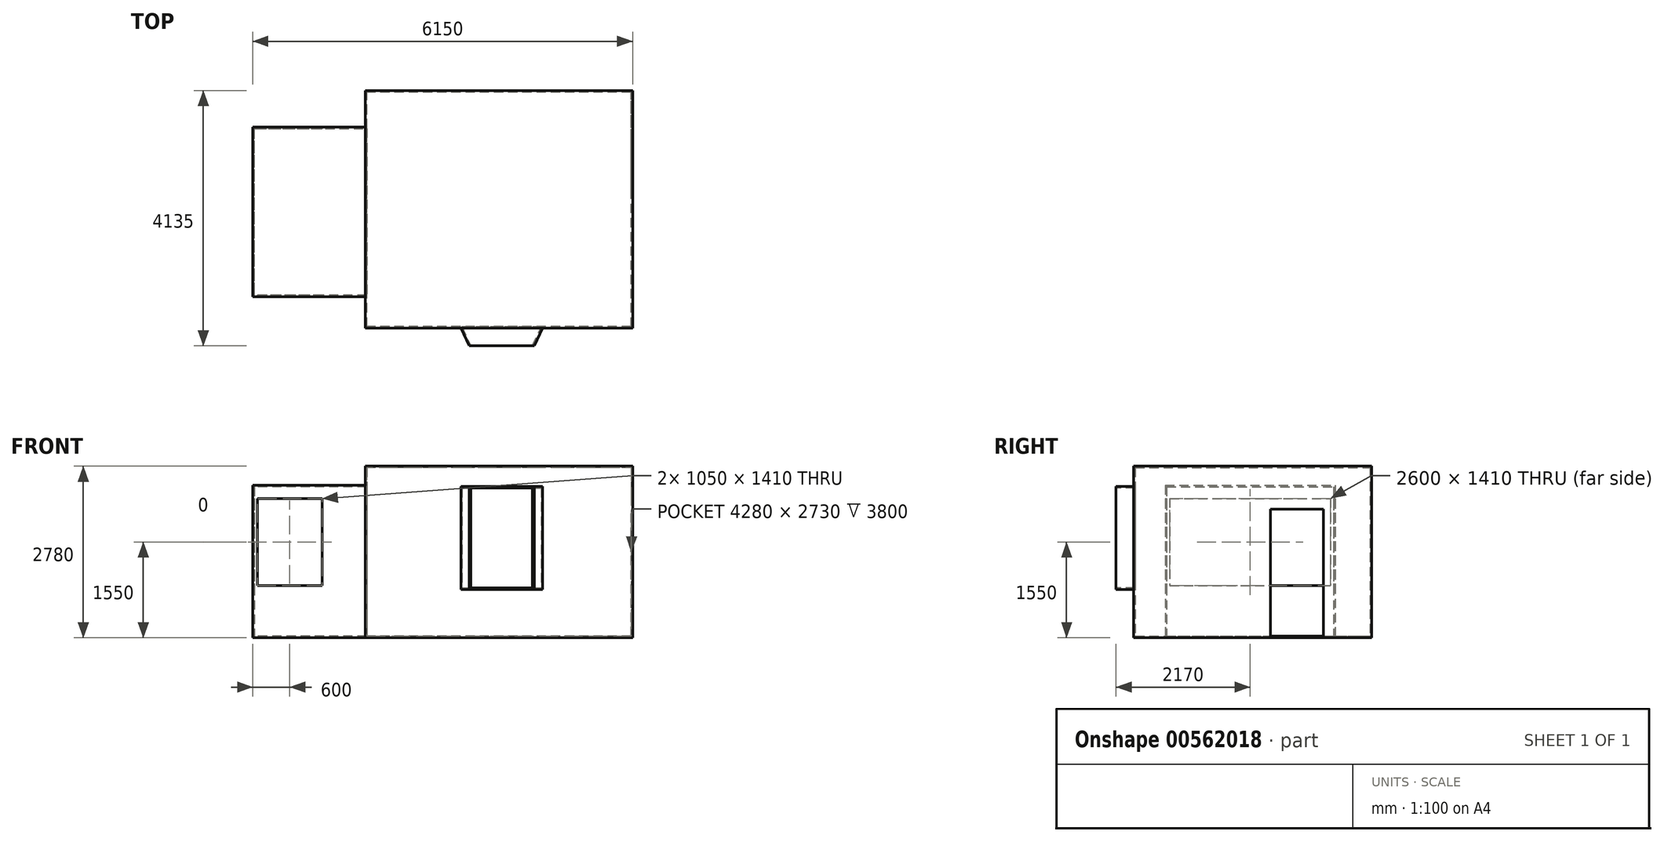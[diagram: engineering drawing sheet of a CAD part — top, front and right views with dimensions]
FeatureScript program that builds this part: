
annotation { "Feature Type Name" : "Feature", "Feature Type Description" : "" }
export const myFeature = defineFeature(function(context is Context, id is Id, definition is map)
    precondition{}
    {
        {
            var Q0;
            Q0=qCreatedBy(makeId("Top.planeOp"),FACE);
            var sketch = newSketch(context, id + "F0", { "sketchPlane" : qUnion([Q0])});
            skLineSegment(sketch, "E0.bottom", {"start": v(0, 0) * mm, "end": v(-1450, 0) * mm});
            skLineSegment(sketch, "E0.top", {"start": v(0, 3800) * mm, "end": v(-4280, 3800) * mm});
            skLineSegment(sketch, "E0.left", {"start": v(0, 0) * mm, "end": v(0, 3800) * mm});
            skLineSegment(sketch, "E0.right", {"start": v(-4280, 0) * mm, "end": v(-4280, 510) * mm});
            skLineSegment(sketch, "E1", {"start": v(-4280, 510) * mm, "end": v(-6100, 510) * mm});
            skLineSegment(sketch, "E2", {"start": v(-6100, 510) * mm, "end": v(-6100, 3210) * mm});
            skLineSegment(sketch, "E3", {"start": v(-6100, 3210) * mm, "end": v(-4280, 3210) * mm});
            skLineSegment(sketch, "E4.trimOffspring", {"start": v(-4280, 3210) * mm, "end": v(-4280, 3800) * mm});
            skLineSegment(sketch, "E5", {"start": v(-2740, 0) * mm, "end": v(-2595, -310) * mm});
            skLineSegment(sketch, "E6", {"start": v(-2595, -310) * mm, "end": v(-1595, -310) * mm});
            skLineSegment(sketch, "E7", {"start": v(-1595, -310) * mm, "end": v(-1450, 0) * mm});
            skLineSegment(sketch, "E8.trimOffspring", {"start": v(-2740, 0) * mm, "end": v(-4280, 0) * mm});
            skSolve(sketch);
        }
        {
            var Q0;
            Q0=makeQuery(id+"F0.imprint","IMPRINT",FACE,{"disambiguationData":[TD([[makeQuery(id+"F0.imprint","IMPRINT",EDGE,{"derivedFrom":sQuery(id+"F0.wireOp",EDGE,"E0.bottom")}),-1.0]])]});
            extrude(context, id + "F1", {"entities" : qUnion([Q0]), "depth" : 2730 * mm, "offsetDistance" : 25 * mm});
        }
        {
            var Q0;
            Q0=makeQuery(id+"F1.opExtrude","CAP_FACE",FACE,{"disambiguationData":[OSD([sQuery(id+"F0.wireOp",EDGE,"E0.bottom"),sQuery(id+"F0.wireOp",EDGE,"E0.top"),sQuery(id+"F0.wireOp",EDGE,"E0.left"),sQuery(id+"F0.wireOp",EDGE,"E0.right"),sQuery(id+"F0.wireOp",EDGE,"E1"),sQuery(id+"F0.wireOp",EDGE,"E2"),sQuery(id+"F0.wireOp",EDGE,"E3"),sQuery(id+"F0.wireOp",EDGE,"E4.trimOffspring"),sQuery(id+"F0.wireOp",EDGE,"E5"),sQuery(id+"F0.wireOp",EDGE,"E6"),sQuery(id+"F0.wireOp",EDGE,"E7"),sQuery(id+"F0.wireOp",EDGE,"E8.trimOffspring")])],"isStart":true});
            var sketch = newSketch(context, id + "F2", { "sketchPlane" : qUnion([Q0])});
            skLineSegment(sketch, "E9", {"start": v(-2740, 0) * mm, "end": v(-1450, 0) * mm});
            skLineSegment(sketch, "E10", {"start": v(-1450, 0) * mm, "end": v(-1595, 310) * mm});
            skLineSegment(sketch, "E11", {"start": v(-1595, 310) * mm, "end": v(-2595, 310) * mm});
            skLineSegment(sketch, "E12", {"start": v(-2595, 310) * mm, "end": v(-2740, 0) * mm});
            skSolve(sketch);
        }
        {
            var Q0;
            Q0 = qSketchRegion(id + "F2", true);
            var Q1;
            Q1=makeQuery(id+"F2.imprint","IMPRINT",FACE,{"disambiguationData":[TD([[makeQuery(id+"F2.imprint","IMPRINT",EDGE,{"derivedFrom":sQuery(id+"F2.wireOp",EDGE,"E9")}),1.0]])]});
            extrude(context, id + "F3", {"entities" : qUnion([Q0, Q1]), "operationType" : NewBodyOperationType.REMOVE, "oppositeDirection" : true, "depth" : 780 * mm, "offsetDistance" : 25 * mm});
        }
        {
            var Q0;
            Q0=makeQuery(id+"F1.opExtrude","CAP_FACE",FACE,{"disambiguationData":[OSD([sQuery(id+"F0.wireOp",EDGE,"E0.bottom"),sQuery(id+"F0.wireOp",EDGE,"E0.top"),sQuery(id+"F0.wireOp",EDGE,"E0.left"),sQuery(id+"F0.wireOp",EDGE,"E0.right"),sQuery(id+"F0.wireOp",EDGE,"E1"),sQuery(id+"F0.wireOp",EDGE,"E2"),sQuery(id+"F0.wireOp",EDGE,"E3"),sQuery(id+"F0.wireOp",EDGE,"E4.trimOffspring"),sQuery(id+"F0.wireOp",EDGE,"E5"),sQuery(id+"F0.wireOp",EDGE,"E6"),sQuery(id+"F0.wireOp",EDGE,"E7"),sQuery(id+"F0.wireOp",EDGE,"E8.trimOffspring")])],"isStart":true});
            cPlane(context, id + "F4", {"entities" : qUnion([Q0]), "cplaneType" : CPlaneType.OFFSET, "offset" : 2400 * mm, "oppositeDirection" : true, "width" : 150 * mm, "height" : 150 * mm});
        }
        {
            var Q0;
            Q0=qCreatedBy(id+"F4.planeOp",FACE);
            var sketch = newSketch(context, id + "F5", { "sketchPlane" : qUnion([Q0])});
            skLineSegment(sketch, "E13.0", {"start": v(-2740, 0) * mm, "end": v(-2595, 310) * mm});
            skLineSegment(sketch, "E14.0", {"start": v(-2595, 310) * mm, "end": v(-1595, 310) * mm});
            skLineSegment(sketch, "E15.0", {"start": v(-1595, 310) * mm, "end": v(-1450, 0) * mm});
            skLineSegment(sketch, "E16", {"start": v(-2740, 0) * mm, "end": v(-1450, 0) * mm});
            skSolve(sketch);
        }
        {
            var Q0;
            Q0 = qSketchRegion(id + "F5", true);
            extrude(context, id + "F6", {"entities" : qUnion([Q0]), "operationType" : NewBodyOperationType.REMOVE, "endBound" : BoundingType.UP_TO_NEXT, "oppositeDirection" : true, "depth" : 25 * mm, "offsetDistance" : 25 * mm});
        }
        {
            var Q0;
            Q0=makeQuery(id+"F1.opExtrude","CAP_FACE",FACE,{"disambiguationData":[OSD([sQuery(id+"F0.wireOp",EDGE,"E0.bottom"),sQuery(id+"F0.wireOp",EDGE,"E0.top"),sQuery(id+"F0.wireOp",EDGE,"E0.left"),sQuery(id+"F0.wireOp",EDGE,"E0.right"),sQuery(id+"F0.wireOp",EDGE,"E1"),sQuery(id+"F0.wireOp",EDGE,"E2"),sQuery(id+"F0.wireOp",EDGE,"E3"),sQuery(id+"F0.wireOp",EDGE,"E4.trimOffspring"),sQuery(id+"F0.wireOp",EDGE,"E5"),sQuery(id+"F0.wireOp",EDGE,"E6"),sQuery(id+"F0.wireOp",EDGE,"E7"),sQuery(id+"F0.wireOp",EDGE,"E8.trimOffspring")])],"isStart":true});
            cPlane(context, id + "F7", {"entities" : qUnion([Q0]), "cplaneType" : CPlaneType.OFFSET, "offset" : 2420 * mm, "oppositeDirection" : true, "width" : 150 * mm, "height" : 150 * mm});
        }
        {
            var Q0;
            Q0=qCreatedBy(id+"F7.planeOp",FACE);
            var sketch = newSketch(context, id + "F8", { "sketchPlane" : qUnion([Q0])});
            skLineSegment(sketch, "E17.0", {"start": v(-6100, -510) * mm, "end": v(-6100, -3210) * mm});
            skLineSegment(sketch, "E18.0", {"start": v(-4280, -510) * mm, "end": v(-6100, -510) * mm});
            skLineSegment(sketch, "E19.0", {"start": v(-6100, -3210) * mm, "end": v(-4280, -3210) * mm});
            skLineSegment(sketch, "E20", {"start": v(-4280, -3210) * mm, "end": v(-4280, -510) * mm});
            skSolve(sketch);
        }
        {
            var Q0;
            Q0 = qSketchRegion(id + "F8", true);
            extrude(context, id + "F9", {"entities" : qUnion([Q0]), "operationType" : NewBodyOperationType.REMOVE, "endBound" : BoundingType.UP_TO_NEXT, "oppositeDirection" : true, "depth" : 25 * mm, "offsetDistance" : 25 * mm});
        }
        {
            var Q0;
            Q0=makeQuery(id+"F1.opExtrude","SWEPT_FACE",FACE,{"disambiguationData":[OSD([sQuery(id+"F0.wireOp",EDGE,"E6")])]});
            shell(context, id + "F10", {"entities" : qUnion([Q0]), "thickness" : 25 * mm, "oppositeDirection" : true});
        }
        {
            var Q0;
            Q0=makeQuery(id+"F1.opExtrude","SWEPT_FACE",FACE,{"disambiguationData":[OSD([sQuery(id+"F0.wireOp",EDGE,"E0.left")])]});
            var sketch = newSketch(context, id + "F11", { "sketchPlane" : qUnion([Q0])});
            skLineSegment(sketch, "E21.bottom", {"start": v(2190, 0) * mm, "end": v(3050, 0) * mm});
            skLineSegment(sketch, "E21.top", {"start": v(2190, 2060) * mm, "end": v(3050, 2060) * mm});
            skLineSegment(sketch, "E21.left", {"start": v(2190, 0) * mm, "end": v(2190, 2060) * mm});
            skLineSegment(sketch, "E21.right", {"start": v(3050, 0) * mm, "end": v(3050, 2060) * mm});
            skLineSegment(sketch, "E22.0.1", {"start": v(3800, 0) * mm, "end": v(3800, 2730) * mm});
            skLineSegment(sketch, "E22.0.3", {"start": v(3800, 2730) * mm, "end": v(3800, 0) * mm, "construction": true});
            skSolve(sketch);
        }
        {
            var Q0;
            Q0=makeQuery(id+"F11.imprint","IMPRINT",FACE,{"disambiguationData":[TD([[makeQuery(id+"F11.imprint","IMPRINT",EDGE,{"derivedFrom":sQuery(id+"F11.wireOp",EDGE,"E21.bottom")}),1.0]])]});
            extrude(context, id + "F12", {"entities" : qUnion([Q0]), "operationType" : NewBodyOperationType.REMOVE, "endBound" : BoundingType.UP_TO_NEXT, "oppositeDirection" : true, "depth" : 25 * mm, "offsetDistance" : 25 * mm});
        }
        {
            var Q0;
            Q0=makeQuery(id+"F10.opShell","OFFSET_FACE",FACE,{"disambiguationData":[OSD([sQuery(id+"F0.wireOp",EDGE,"E2")])]});
            var sketch = newSketch(context, id + "F13", { "sketchPlane" : qUnion([Q0])});
            skLineSegment(sketch, "E23.bottom", {"start": v(560, 2230) * mm, "end": v(3160, 2230) * mm});
            skLineSegment(sketch, "E23.top", {"start": v(560, 820) * mm, "end": v(3160, 820) * mm});
            skLineSegment(sketch, "E23.left", {"start": v(560, 2230) * mm, "end": v(560, 820) * mm});
            skLineSegment(sketch, "E23.right", {"start": v(3160, 2230) * mm, "end": v(3160, 820) * mm});
            skSolve(sketch);
        }
        {
            var Q0;
            Q0 = qSketchRegion(id + "F13", true);
            extrude(context, id + "F14", {"entities" : qUnion([Q0]), "operationType" : NewBodyOperationType.REMOVE, "endBound" : BoundingType.UP_TO_NEXT, "oppositeDirection" : true, "depth" : 25 * mm, "offsetDistance" : 25 * mm});
        }
        {
            var Q0;
            Q0=makeQuery(id+"F10.opShell","OFFSET_FACE",FACE,{"disambiguationData":[OSD([sQuery(id+"F0.wireOp",EDGE,"E3")])]});
            var sketch = newSketch(context, id + "F15", { "sketchPlane" : qUnion([Q0])});
            skLineSegment(sketch, "E24.bottom", {"start": v(-6050, 2230) * mm, "end": v(-5000, 2230) * mm});
            skLineSegment(sketch, "E24.top", {"start": v(-6050, 820) * mm, "end": v(-5000, 820) * mm});
            skLineSegment(sketch, "E24.left", {"start": v(-6050, 2230) * mm, "end": v(-6050, 820) * mm});
            skLineSegment(sketch, "E24.right", {"start": v(-5000, 2230) * mm, "end": v(-5000, 820) * mm});
            skSolve(sketch);
        }
        {
            var Q0;
            Q0 = qSketchRegion(id + "F15", true);
            extrude(context, id + "F16", {"entities" : qUnion([Q0]), "operationType" : NewBodyOperationType.REMOVE, "endBound" : BoundingType.UP_TO_NEXT, "oppositeDirection" : true, "depth" : 25 * mm, "offsetDistance" : 25 * mm});
        }
        {
            var Q0;
            Q0=makeQuery(id+"F10.opShell","OFFSET_FACE",FACE,{"disambiguationData":[OSD([sQuery(id+"F0.wireOp",EDGE,"E1")])]});
            var sketch = newSketch(context, id + "F17", { "sketchPlane" : qUnion([Q0])});
            skLineSegment(sketch, "E25.bottom", {"start": v(5000, 2230) * mm, "end": v(6050, 2230) * mm});
            skLineSegment(sketch, "E25.top", {"start": v(5000, 820) * mm, "end": v(6050, 820) * mm});
            skLineSegment(sketch, "E25.left", {"start": v(5000, 2230) * mm, "end": v(5000, 820) * mm});
            skLineSegment(sketch, "E25.right", {"start": v(6050, 2230) * mm, "end": v(6050, 820) * mm});
            skSolve(sketch);
        }
        {
            var Q0;
            Q0=makeQuery(id+"F17.imprint","IMPRINT",FACE,{"disambiguationData":[TD([[makeQuery(id+"F17.imprint","IMPRINT",EDGE,{"derivedFrom":sQuery(id+"F17.wireOp",EDGE,"E25.bottom")}),-1.0]])]});
            extrude(context, id + "F18", {"entities" : qUnion([Q0]), "operationType" : NewBodyOperationType.REMOVE, "endBound" : BoundingType.UP_TO_NEXT, "oppositeDirection" : true, "depth" : 25 * mm, "offsetDistance" : 25 * mm});
        }
    });
